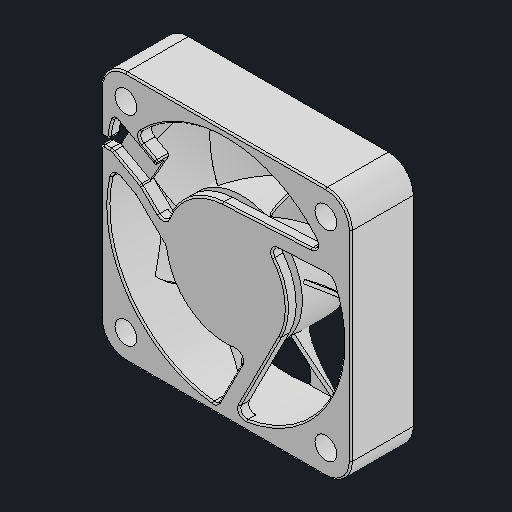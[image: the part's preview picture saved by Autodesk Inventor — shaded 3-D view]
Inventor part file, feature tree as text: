
AUTODESK INVENTOR PART (.ipt)
format: ipt  version: 2024.2 (Build 282272000, 272)  size: 711,680 bytes
history: native  units: mm
features: other x2, fillet x1, boolean_combine x1
ambient origin geometry x8: Origin, YZ Plane, XZ Plane, XY Plane, X Axis, Y Axis, Z Axis, Center Point
bodies: Body1 (feature_tree), Body2 (feature_tree)
feature tree (4):
  other  "솔리드1"
  other  "솔리드2"
  fillet  "Fillet5"  [1 undecoded]
  boolean_combine  "Combine1"
note: 1 required parameter value undecoded (feature->parameter linkage not recoverable at this tier; creation-order binding heuristic only, values carry confidence <= 0.55)
